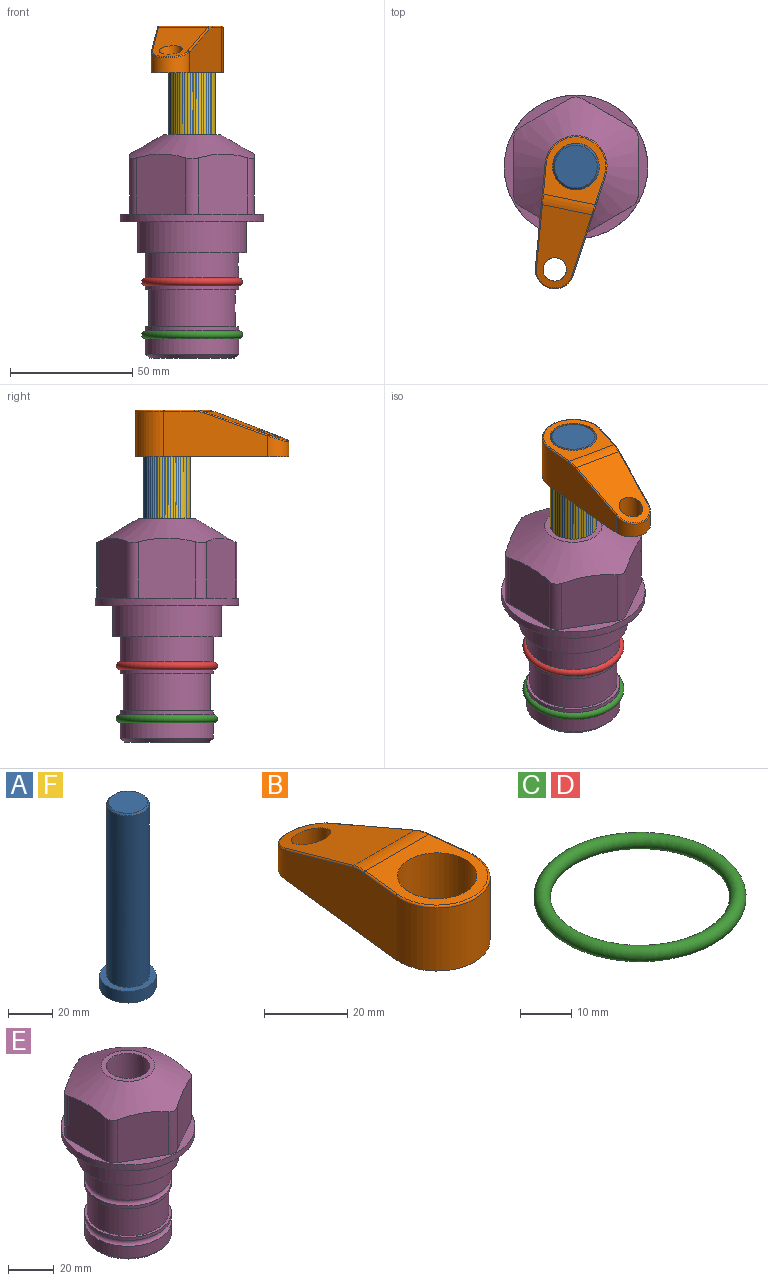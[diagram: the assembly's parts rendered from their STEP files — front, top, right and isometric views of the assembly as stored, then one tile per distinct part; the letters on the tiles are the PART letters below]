
ASSEMBLY  parts=6 mates=3
PART A: 6 faces, bbox 25.4x25.4x101.6 mm
  f0: plane 17.46x17.46mm, normal (0,0,1), area 239.5mm2, adj f5
  f1: plane 25.4x25.4mm, normal (0,0,-1), area 506.7mm2, adj f2
  f2: cylinder r=12.7mm len=25.4mm, axis (0,0,1), area 506.7mm2, adj f1,f3
  f3: plane 25.4x25.4mm, normal (0,0,1), area 221.7mm2, adj f2,f4
  f4: cylinder r=9.53mm len=94.46mm, axis (0,0,1), area 5653mm2, adj f3,f5
  f5: cone r=8.73mm half-angle=45deg, axis (0,0,-1), area 64.4mm2, adj f0,f4
PART B: 44 faces, bbox 27.5x64.5x19.1 mm
  f0: plane 2.3x0.95mm, normal (0,0,-1), area 1mm2, adj f25,f30,f34
  f1: plane 63.5x25.4mm, normal (0,0,-1), area 561.7mm2, adj f2,f3,f4,f5,f6,f7,f19,f20
  f2: cylinder r=12.7mm len=25.4mm, axis (0,0,-1), area 792.2mm2, adj f1,f3,f5,f13
  f3: plane 42.33x18.54mm, normal (0.99,0.11,0), area 647mm2, adj f1,f2,f4,f11,f12,f14
  f4: cylinder r=7.94mm len=15.78mm, axis (0,0,-1), area 158.6mm2, adj f1,f3,f5,f16
  f5: plane 42.33x18.54mm, normal (-0.99,0.11,0), area 647mm2, adj f1,f2,f4,f15,f17,f18
  f6: cylinder r=9.53mm len=19.05mm, axis (0,0,-1), area 1140.1mm2, adj f1,f8
  f7: cylinder r=4.76mm len=10.98mm, axis (0,0,-1), area 276.1mm2, adj f1,f9
  f8: plane 25.83x24.38mm, normal (0,0,1), area 262.2mm2, adj f6,f10,f11,f13,f15
  f9: plane 32.49x20.55mm, normal (0,0.34,0.94), area 489.9mm2, adj f7,f10,f14,f16,f18
  f10: cylinder r=12.7mm len=21.49mm, axis (-1,0,0), area 93.2mm2, adj f8,f9,f12,f17
  f11: cylinder r=0.51mm len=12.34mm, axis (0.11,-0.99,0), area 9.9mm2, adj f3,f8,f12,f13
  f12: bspline ~7.62x1.64mm, area 3.5mm2, adj f3,f10,f11,f14
  f13: torus R=12.19mm, axis (0,0,1), area 33.6mm2, adj f2,f8,f11,f15
  f14: cylinder r=0.51mm len=26.01mm, axis (0.1,-0.93,0.34), area 21.6mm2, adj f3,f9,f12,f16
  f15: cylinder r=0.51mm len=12.34mm, axis (0.11,0.99,0), area 9.9mm2, adj f5,f8,f13,f17
  f16: bspline ~15.78x7.05mm, area 15.7mm2, adj f4,f9,f14,f18
  f17: bspline ~7.62x1.64mm, area 3.5mm2, adj f5,f10,f15,f18
  f18: cylinder r=0.51mm len=26.01mm, axis (0.1,0.93,-0.34), area 21.6mm2, adj f5,f9,f16,f17
  f19: plane 21.6x14.29mm, normal (-0.99,-0.11,0), area 242.6mm2, adj f1,f26,f28,f34,f36,f38
  f20: plane 21.6x14.29mm, normal (0.99,-0.11,0), area 242.6mm2, adj f1,f27,f29,f37,f39,f41
  f21: cylinder r=12.7mm len=14.29mm, axis (0,0,-1), area 173.2mm2, adj f1,f26,f27,f30,f31,f33
  f22: cylinder r=7.94mm len=7.63mm, axis (0,0,-1), area 53.8mm2, adj f1,f28,f29,f42
  f23: plane 2.3x0.95mm, normal (0,0,-1), area 1mm2, adj f25,f33,f37
  f24: plane 17.94x12.32mm, normal (0,-0.34,-0.94), area 191.2mm2, adj f25,f38,f41,f42
  f25: cylinder r=9.53mm len=12.93mm, axis (-1,0,0), area 37.5mm2, adj f0,f23,f24,f31,f36,f39
  f26: cylinder r=1.59mm len=14.29mm, axis (0,0,-1), area 49mm2, adj f1,f19,f21,f32
  f27: cylinder r=1.59mm len=14.29mm, axis (0,0,-1), area 49mm2, adj f1,f20,f21,f35
  f28: cylinder r=1.59mm len=7.28mm, axis (0,0,-1), area 22.1mm2, adj f1,f19,f22,f40
  f29: cylinder r=1.59mm len=7.28mm, axis (0,0,-1), area 22.1mm2, adj f1,f20,f22,f43
  f30: torus R=14.29mm, axis (0,0,1), area 5.8mm2, adj f0,f21,f31,f32
  f31: bspline ~11.06x2.73mm, area 20.8mm2, adj f21,f25,f30,f33
  f32: sphere r=1.59mm, area 5.4mm2, adj f26,f30,f34
  f33: torus R=14.29mm, axis (0,0,1), area 5.8mm2, adj f21,f23,f31,f35
  f34: cylinder r=1.59mm len=1.68mm, axis (-0.11,0.99,0), area 2.4mm2, adj f0,f19,f32,f36
  f35: sphere r=1.59mm, area 5.4mm2, adj f27,f33,f37
  f36: bspline ~5.82x2.33mm, area 7.7mm2, adj f19,f25,f34,f38
  f37: cylinder r=1.59mm len=1.68mm, axis (0.11,0.99,0), area 2.4mm2, adj f20,f23,f35,f39
  f38: cylinder r=1.59mm len=18.33mm, axis (0.1,-0.93,0.34), area 46.7mm2, adj f19,f24,f36,f40
  f39: bspline ~5.82x2.33mm, area 7.7mm2, adj f20,f25,f37,f41
  f40: sphere r=1.59mm, area 3.6mm2, adj f28,f38,f42
  f41: cylinder r=1.59mm len=18.33mm, axis (0.1,0.93,-0.34), area 46.7mm2, adj f20,f24,f39,f43
  f42: bspline ~8.31x1.84mm, area 15.3mm2, adj f22,f24,f40,f43
  f43: sphere r=1.59mm, area 3.6mm2, adj f29,f41,f42
PART C: 1 faces, bbox 44.7x44.7x3.2 mm
  f0: torus R=19.05mm, axis (0,0,1), area 1193.9mm2
PART D: same geometry as C
PART E: 36 faces, bbox 58.7x58.7x91.2 mm
  f0: cylinder r=17.78mm len=35.56mm, axis (0,0,1), area 1670.8mm2, adj f23,f24,f31
  f1: cylinder r=19.05mm len=38.1mm, axis (0,0,1), area 1191.9mm2, adj f26,f27,f30
  f2: plane 58.66x58.66mm, normal (0,0,-1), area 1150.6mm2, adj f3,f28
  f3: cylinder r=29.33mm len=58.66mm, axis (0,0,-1), area 585.1mm2, adj f2,f4
  f4: plane 58.66x58.66mm, normal (0,0,1), area 475.9mm2, adj f3,f5,f6,f7,f8,f9,f10,f11
  f5: plane 24.5x20.32mm, normal (0.5,-0.87,0), area 562.8mm2, adj f4,f15,f16,f17
  f6: plane 24.5x20.32mm, normal (-0.5,-0.87,0), area 562.8mm2, adj f4,f14,f15,f17
  f7: plane 24.5x23.48mm, normal (-1,0,0), area 562.8mm2, adj f4,f13,f14,f17
  f8: plane 24.5x20.32mm, normal (-0.5,0.87,0), area 562.8mm2, adj f4,f12,f13,f17
  f9: plane 24.5x20.32mm, normal (0.5,0.87,0), area 562.8mm2, adj f4,f11,f12,f17
  f10: plane 24.5x23.48mm, normal (1,0,0), area 562.8mm2, adj f4,f11,f16,f17
  f11: cylinder r=5.08mm len=23.01mm, axis (0,0,-1), area 121.2mm2, adj f4,f9,f10,f17
  f12: cylinder r=5.08mm len=23.01mm, axis (0,0,-1), area 121.2mm2, adj f4,f8,f9,f17
  f13: cylinder r=5.08mm len=23.01mm, axis (0,0,-1), area 121.2mm2, adj f4,f7,f8,f17
  f14: cylinder r=5.08mm len=23.01mm, axis (0,0,-1), area 121.2mm2, adj f4,f6,f7,f17
  f15: cylinder r=5.08mm len=23.01mm, axis (0,0,-1), area 121.2mm2, adj f4,f5,f6,f17
  f16: cylinder r=5.08mm len=23.01mm, axis (0,0,-1), area 121.2mm2, adj f4,f5,f10,f17
  f17: cone r=11.73mm half-angle=60deg, axis (0,0,-1), area 2071.8mm2, adj f5,f6,f7,f8,f9,f10,f11,f12
  f18: plane 23.46x23.46mm, normal (0,0,1), area 147.4mm2, adj f17,f35
  f19: plane 34.93x34.93mm, normal (0,0,-1), area 958mm2, adj f29
  f20: cylinder r=19.05mm len=38.1mm, axis (0,0,1), area 760.1mm2, adj f21,f29
  f21: torus R=19.05mm, axis (0,0,1), area 565.3mm2, adj f20,f22
  f22: cylinder r=19.05mm len=38.1mm, axis (0,0,1), area 190mm2, adj f21,f23
  f23: plane 38.1x38.1mm, normal (0,0,1), area 146.9mm2, adj f0,f22
  f24: plane 38.1x38.1mm, normal (0,0,-1), area 146.9mm2, adj f0,f25
  f25: cylinder r=19.05mm len=38.1mm, axis (0,0,1), area 190mm2, adj f24,f26
  f26: torus R=19.05mm, axis (0,0,1), area 565.3mm2, adj f1,f25
  f27: plane 44.45x44.45mm, normal (0,0,-1), area 411.7mm2, adj f1,f28
  f28: cylinder r=22.23mm len=44.45mm, axis (0,0,1), area 1773.5mm2, adj f2,f27
  f29: cone r=19.05mm half-angle=45deg, axis (0,0,1), area 257.5mm2, adj f19,f20
  f30: cylinder r=3.17mm len=6.75mm, axis (-1,0,0), area 128mm2, adj f1,f33
  f31: cylinder r=3.17mm len=6.35mm, axis (-1,0,0), area 102.5mm2, adj f0,f33
  f32: plane 25.4x25.4mm, normal (0,0,1), area 506.7mm2, adj f33
  f33: cylinder r=12.7mm len=66.42mm, axis (0,0,-1), area 5236.2mm2, adj f30,f31,f32,f34
  f34: cone r=9.53mm half-angle=30deg, axis (0,0,-1), area 443.4mm2, adj f33,f35
  f35: cylinder r=9.53mm len=19.05mm, axis (0,0,-1), area 849mm2, adj f18,f34
PART F: same geometry as A
PLACE A rot(axis=(0,0,-1),101.7deg) t=(0,0,6.38)mm
PLACE B rot(axis=(0,0,1),168.3deg) t=(0,0,60.99)mm
PLACE C t=(0,0,-21.59)mm
PLACE D at identity
PLACE E at identity fixed
PLACE F at identity
MATE fastened C.f0 <-> E.f0  axis (0,0,1) through (0,0,-46.1)mm
MATE cylindrical A.f2 <-> E.f0  axis (0,0,1) through (0,0,32.01)mm
MATE fastened B.f2 <-> A.f2  axis (0,0,1) through (0,0,80.04)mm
